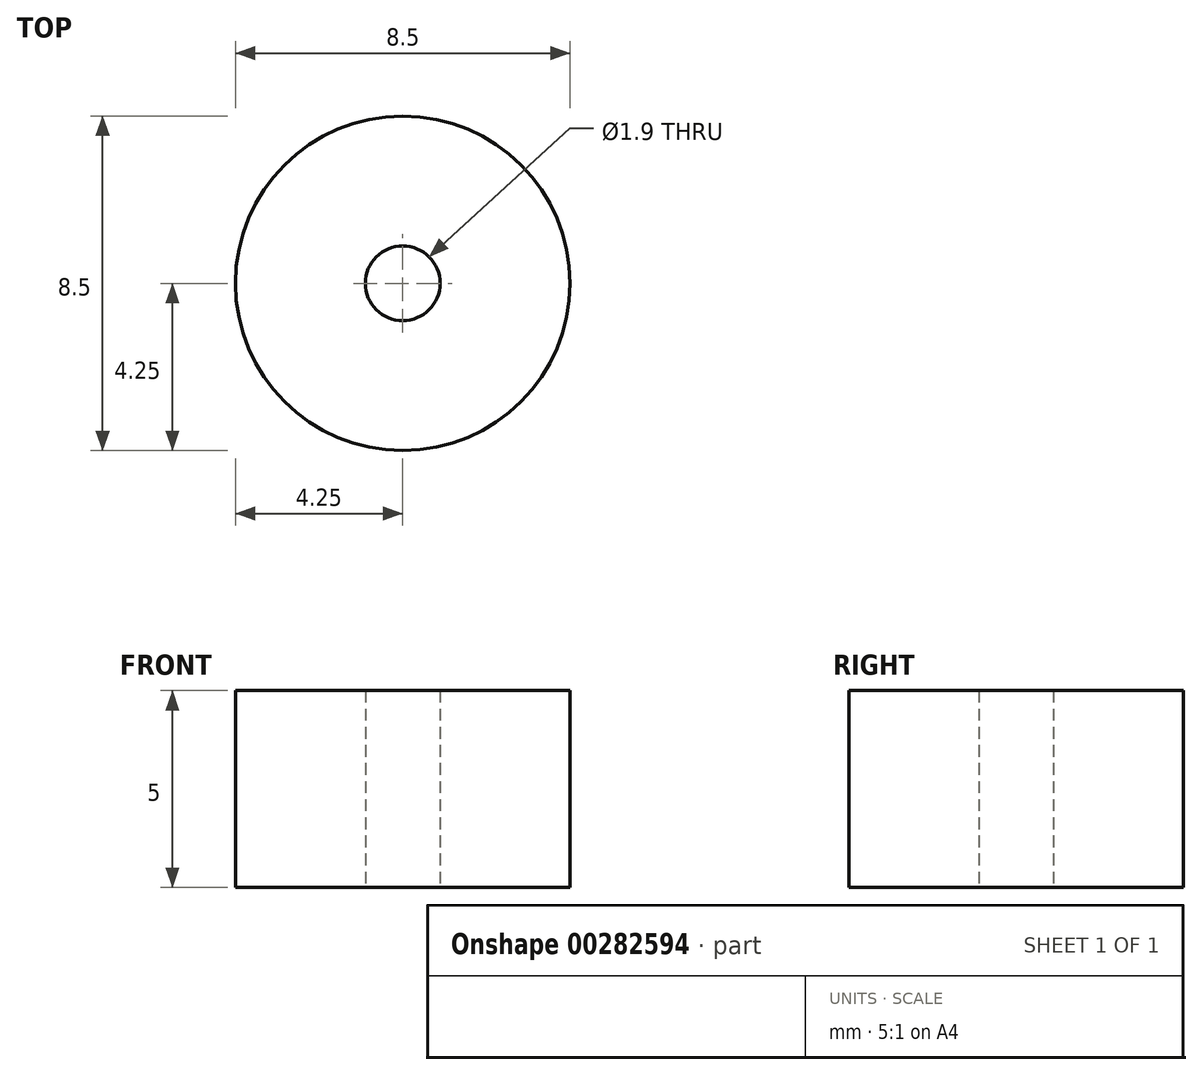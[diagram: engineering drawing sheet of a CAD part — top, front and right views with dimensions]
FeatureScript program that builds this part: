
annotation { "Feature Type Name" : "Feature", "Feature Type Description" : "" }
export const myFeature = defineFeature(function(context is Context, id is Id, definition is map)
    precondition{}
    {
        {
            var Q0;
            Q0=qCreatedBy(makeId("Top.planeOp"),FACE);
            var sketch = newSketch(context, id + "F0", { "sketchPlane" : qUnion([Q0])});
            skCircle(sketch, "E0", {"center": v(0, 0) * mm, "radius": 4.25 * mm});
            skCircle(sketch, "E1", {"center": v(0, 0) * mm, "radius": 0.95 * mm});
            skSolve(sketch);
        }
        {
            var Q0;
            Q0=makeQuery(id+"F0.imprint","IMPRINT",FACE,{"disambiguationData":[TD([[makeQuery(id+"F0.imprint","IMPRINT",EDGE,{"derivedFrom":sQuery(id+"F0.wireOp",EDGE,"E0")}),1.0]])]});
            extrude(context, id + "F1", {"entities" : qUnion([Q0]), "depth" : 5 * mm});
        }
    });
